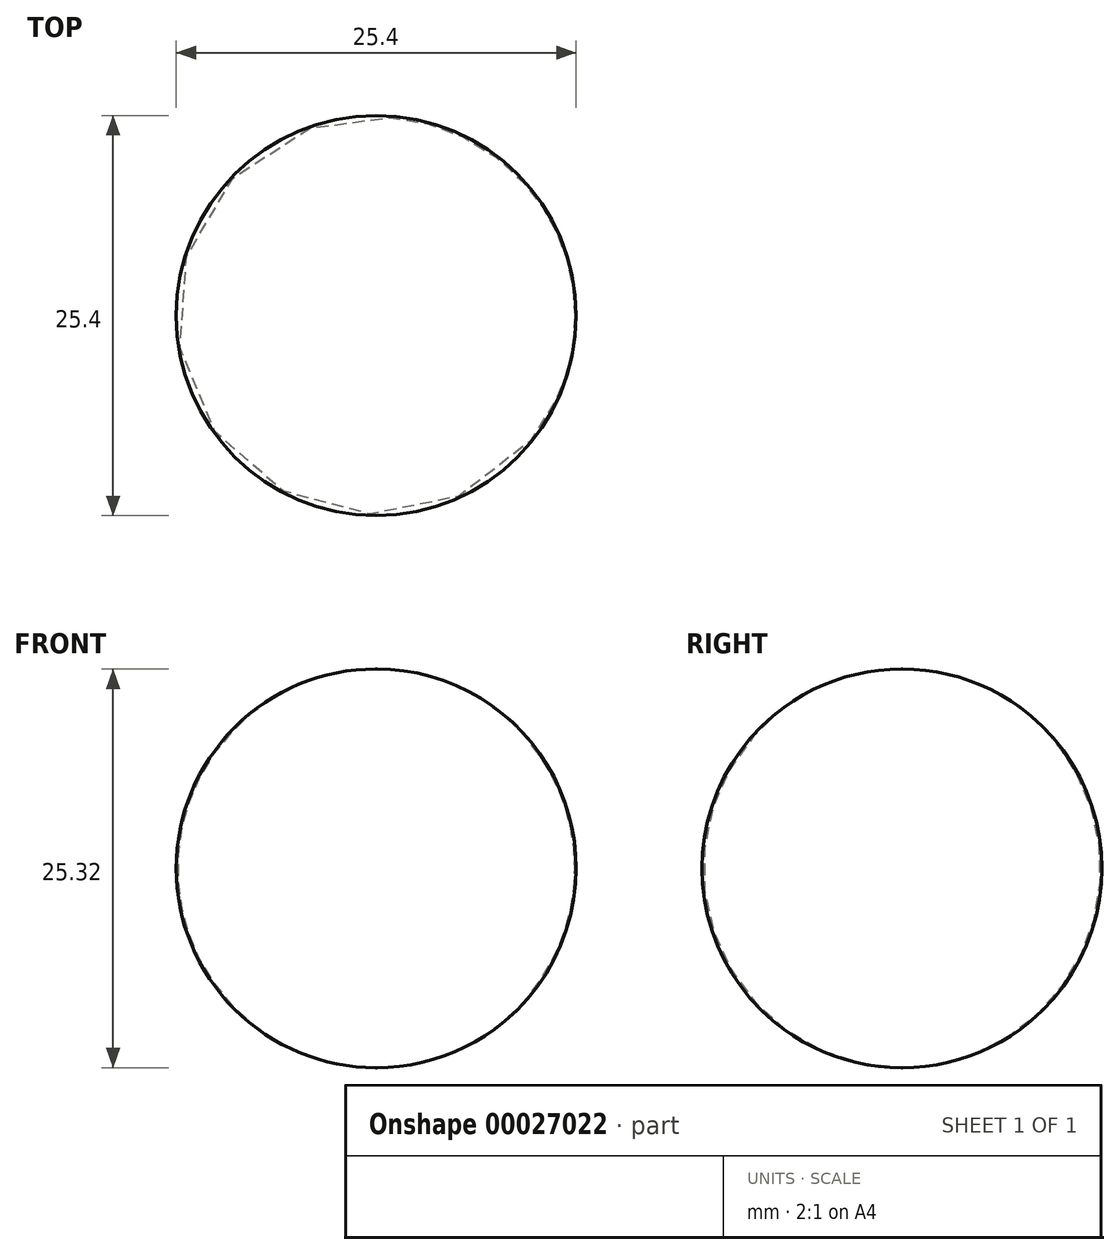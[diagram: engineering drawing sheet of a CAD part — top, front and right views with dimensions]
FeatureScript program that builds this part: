
annotation { "Feature Type Name" : "Feature", "Feature Type Description" : "" }
export const myFeature = defineFeature(function(context is Context, id is Id, definition is map)
    precondition{}
    {
        {
            var Q0;
            Q0=qCreatedBy(makeId("Front.planeOp"),FACE);
            var sketch = newSketch(context, id + "F0", { "sketchPlane" : qUnion([Q0])});
            skLineSegment(sketch, "E0", {"start": v(0, 0) * mm, "end": v(0, 12.66) * mm});
            skLineSegment(sketch, "E1", {"start": v(0, 0) * mm, "end": v(0, -12.66) * mm});
            skArc(sketch, "E2", {"start": v(0, 12.66) * mm, "mid": v(-12.7, 0) * mm, "end": v(0, -12.66) * mm});
            skSolve(sketch);
        }
        {
            var Q0;
            Q0=makeQuery(id+"F0.imprint","IMPRINT",FACE,{"disambiguationData":[TD([[makeQuery(id+"F0.imprint","IMPRINT",EDGE,{"derivedFrom":sQuery(id+"F0.wireOp",EDGE,"E0")}),1.0]])]});
            var Q1;
            Q1=sQuery(id+"F0.wireOp",EDGE,"E0");
            revolve(context, id + "F1", {"entities" : qUnion([Q0]), "axis" : qUnion([Q1]), "revolveType" : RevolveType.FULL});
        }
    });
